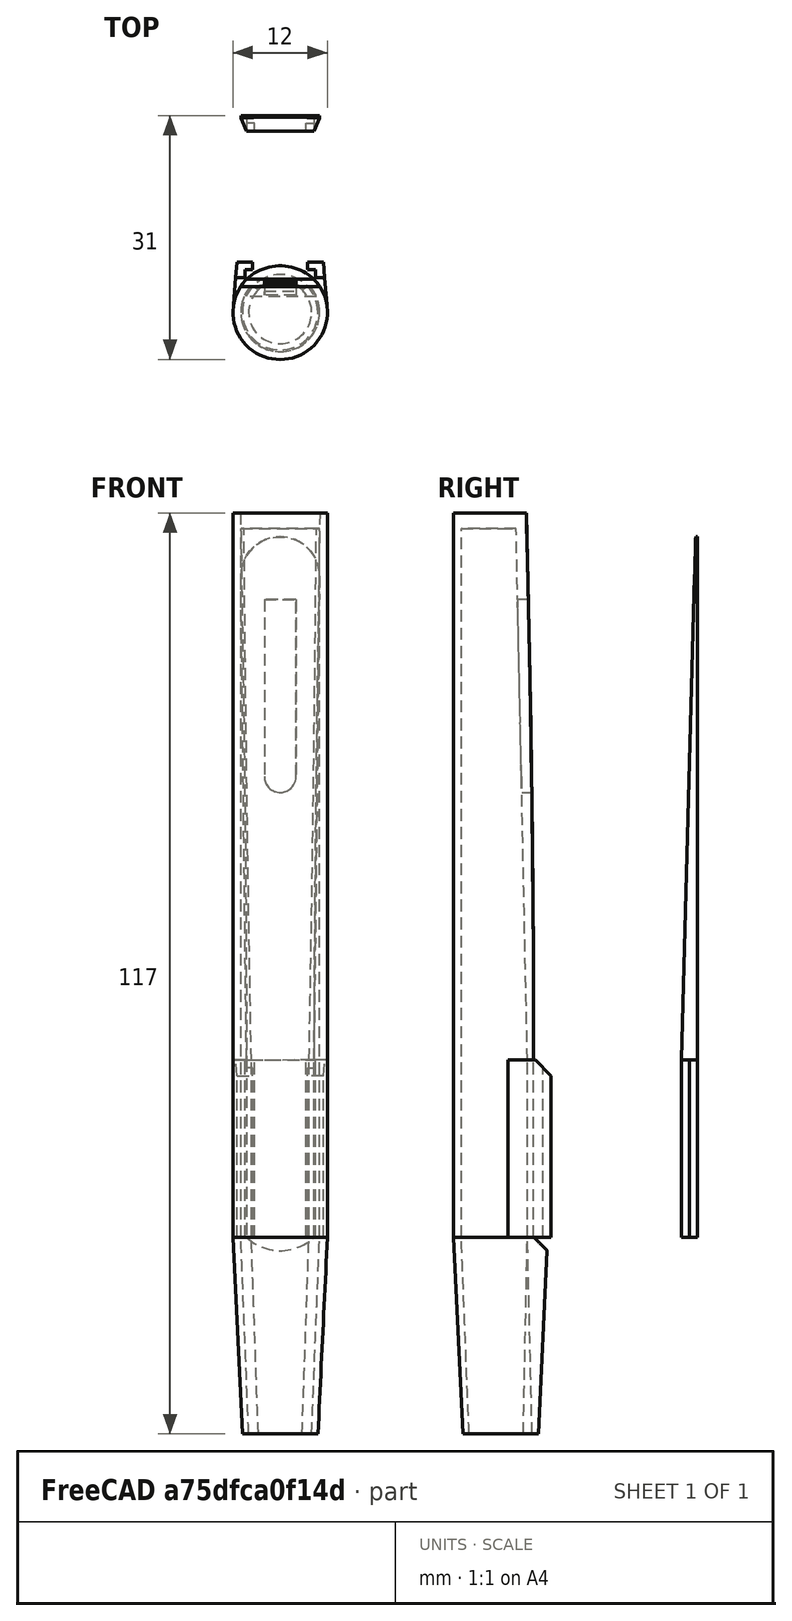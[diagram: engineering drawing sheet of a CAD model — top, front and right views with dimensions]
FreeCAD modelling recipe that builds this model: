
FCSTD DOCUMENT  (FreeCAD 1.0R39319 (Git))
Label: stroik_burd2
License: All rights reserved
LicenseURL: https://en.wikipedia.org/wiki/All_rights_reserved
objects: Sketcher::SketchObject×12, PartDesign::Pocket×6, PartDesign::Pad×4, PartDesign::Body×2, Mesh::Feature×2, Part::FeaturePython×1, PartDesign::FeatureBase×1, App::VarSet×1, PartDesign::Mirrored×1, PartDesign::Plane×1, PartDesign::AdditiveLoft×1, PartDesign::ShapeBinder×1, PartDesign::Chamfer×1
note: 69 computed .brp shape members not serialized (recipe doc carries the construction recipe); baked Part::Feature solids carry a one-line shape summary decoded from their .brp

FEATURE [Part::FeaturePython] Tube  # WARN: FeaturePython — macro-defined, semantics opaque (R4)
  AttacherType = Attacher::AttachEngine3D
  Height = 90
  InnerRadius = 5
  OuterRadius = 6
  Placement = pos=(0,0,0) rot=(0,1,0;1.5708rad)
  expr: Height = VarSet.leaf_len
  expr: InnerRadius = VarSet.d_inner
  expr: OuterRadius = VarSet.d_outer
FEATURE [PartDesign::FeatureBase] BaseFeature
  BaseFeature = -> Tube
  Suppressed = false
FEATURE [App::VarSet] VarSet
  d_inner = 5
  d_outer = 6
  d_outer_plug = 6
  leaf_angle = 0
  leaf_angle2 = 1.55
  leaf_end_thickness = 0.2
  leaf_len = 90
  leaf_start_thickness = 2
  plug_inner_start = 4
  plug_len = 25
  plug_outer_start = 4.8
FEATURE [Sketcher::SketchObject] Sketch
  ArcFitTolerance = 1e-06
  AttachmentSupport = -> [YZ_Plane]
  ExternalGeometry = -> [BaseFeature]
  FullyConstrained = true
  MakeInternals = false
  MapMode = 5
  Placement = pos=(0,0,0) rot=(0.57735,0.57735,0.57735;2.0944rad)
  expr: Constraints[14] = VarSet.leaf_len / 4
  expr: Constraints[8] = VarSet.d_outer * 0.3
  sketch-geometry (6):
    g0: LineSegment StartX=6 StartY=90 StartZ=0 EndX=4.2 EndY=90 EndZ=0
    g1: LineSegment StartX=4.2 StartY=0 StartZ=0 EndX=6 EndY=0 EndZ=0
    g2: LineSegment StartX=6 StartY=0 StartZ=0 EndX=6 EndY=22.5 EndZ=0
    g3: LineSegment StartX=6 StartY=22.5 StartZ=0 EndX=6 EndY=90 EndZ=0
    g4: LineSegment StartX=4.2 StartY=90 StartZ=0 EndX=4.2 EndY=22.5 EndZ=0
    g5: LineSegment StartX=4.2 StartY=22.5 StartZ=0 EndX=4.2 EndY=0 EndZ=0
  constraints (17):
    c: Coincident(g0,g4)
    c: Coincident(g5,g1)
    c: Coincident(g1,g2)
    c: Coincident(g3,g0)
    c: Horizontal(g0)
    c: Horizontal(g1)
    c: Coincident(g0,g-3)
    c: PointOnObject(g5,g-4)
    c: DistanceX(g5,g1) = 1.8
    c: Coincident(g2,g3)
    c: Vertical(g2)
    c: Vertical(g3)
    c: Coincident(g4,g5)
    c: Vertical(g5)
    c: DistanceY(g2,g2) = 22.5
    c: Horizontal(g2,g4)
    c: Vertical(g4)
FEATURE [Sketcher::SketchObject] Sketch001
  ArcFitTolerance = 1e-06
  AttachmentSupport = -> [YZ_Plane]
  ExternalGeometry = -> [Sketch]
  FullyConstrained = true
  MakeInternals = false
  MapMode = 5
  Placement = pos=(0,0,0) rot=(0.57735,0.57735,0.57735;2.0944rad)
  expr: Constraints[12] = 0.8
  expr: Constraints[13] = 3 / 4 * VarSet.leaf_len * tan(VarSet.leaf_angle2) + 0.4 mm
  sketch-geometry (6):
    g0: LineSegment StartX=4.2 StartY=0 StartZ=0 EndX=3.4 EndY=0 EndZ=0
    g1: LineSegment StartX=3.4 StartY=0 StartZ=0 EndX=3.4 EndY=22.5 EndZ=0
    g2: LineSegment StartX=3.4 StartY=22.5 StartZ=0 EndX=1.9735 EndY=90 EndZ=0
    g3: LineSegment StartX=1.9735 StartY=90 StartZ=0 EndX=4.2 EndY=90 EndZ=0
    g4: LineSegment StartX=4.2 StartY=90 StartZ=0 EndX=4.2 EndY=22.5 EndZ=0
    g5: LineSegment StartX=4.2 StartY=22.5 StartZ=0 EndX=4.2 EndY=0 EndZ=0
  constraints (15):
    c: Coincident(g-4,g0)
    c: PointOnObject(g0,g-1)
    c: Coincident(g0,g1)
    c: Vertical(g1)
    c: Coincident(g1,g2)
    c: Coincident(g2,g3)
    c: Coincident(g3,g-3)
    c: Horizontal(g3)
    c: Coincident(g3,g4)
    c: Coincident(g4,g-4)
    c: Coincident(g4,g5)
    c: Coincident(g5,g0)
    c: DistanceX(g1,g4) = 0.8
    c: DistanceX(g2,g3) = 2.2265
    c: Horizontal(g1,g4)
FEATURE [PartDesign::Pocket] Pocket  label="1 ścięcie"
  BaseFeature = -> BaseFeature
  Direction = (-1,0,0)
  Length = 5
  Length2 = 5
  Midplane = true
  Profile = -> Sketch
  ReferenceAxis = -> Sketch [N_Axis]
  Refine = true
  Suppressed = false
  Type = 1
FEATURE [PartDesign::Pad] Pad  label="uzupełnienie"
  AlongSketchNormal = false
  BaseFeature = -> Pocket
  Direction = (1,0,0)
  Length = 13
  Length2 = 10
  Midplane = true
  Profile = -> Sketch001
  ReferenceAxis = -> Sketch001 [N_Axis]
  Refine = true
  Suppressed = false
  Type = 1
  UpToShape = -> [Pocket]
FEATURE [PartDesign::Mirrored] Mirrored
  BaseFeature = -> Pad
  MirrorPlane = -> YZ_Plane
  Originals = -> [Pad]
  Refine = true
  Suppressed = false
  TransformMode = 0
FEATURE [Sketcher::SketchObject] Sketch002
  ArcFitTolerance = 1e-06
  AttachmentSupport = -> [Mirrored]
  ExternalGeometry = -> [Mirrored]
  FullyConstrained = true
  MakeInternals = false
  MapMode = 5
  Placement = pos=(0,4.2,0) rot=(0,0.707107,0.707107;3.14159rad)
  expr: Constraints[10] = 3 / 4 * VarSet.leaf_len / 3
  expr: Constraints[6] = VarSet.d_outer / 3
  expr: Constraints[9] = VarSet.leaf_len / 10
  sketch-geometry (4):
    g0: LineSegment StartX=2.011 StartY=58.5 StartZ=0 EndX=2.011 EndY=81 EndZ=0
    g1: LineSegment StartX=2.011 StartY=81 StartZ=0 EndX=-2.011 EndY=81 EndZ=0
    g2: LineSegment StartX=-2.011 StartY=81 StartZ=0 EndX=-2.011 EndY=58.5 EndZ=0
    g3: ArcOfCircle CenterX=0 CenterY=58.5 CenterZ=0 NormalX=0 NormalY=0 NormalZ=1 AngleXU=0 Radius=2.011 StartAngle=3.14159 EndAngle=6.28319
  constraints (12):
    c: Coincident(g0,g1)
    c: Coincident(g1,g2)
    c: Coincident(g3,g2)
    c: Coincident(g3,g0)
    c: PointOnObject(g3,g-2)
    c: Horizontal(g0,g2)
    c: DistanceX(g0,g-4) = 2
    c: Horizontal(g2,g3)
    c: Symmetric(g0,g1,g-2)
    c: DistanceY(g1,g-7) = 9
    c: DistanceY(g3,g1) = 22.5
    c: Vertical(g1,g2)
FEATURE [PartDesign::Pocket] Pocket001  label="dziurka"
  BaseFeature = -> Mirrored
  Direction = (0,-1,2e-16)
  Length = 2.5
  Length2 = 5
  Profile = -> Sketch002
  ReferenceAxis = -> Sketch002 [N_Axis]
  Refine = true
  Suppressed = false
  Type = 0
  expr: Length = VarSet.d_inner / 2
FEATURE [Sketcher::SketchObject] Sketch003
  ArcFitTolerance = 1e-06
  AttachmentSupport = -> [Pocket001]
  ExternalGeometry = -> [Pocket001]
  FullyConstrained = true
  MakeInternals = false
  MapMode = 5
  Placement = pos=(0,0,90) rot=(0,0,1;0rad)
  sketch-geometry (2):
    g0: ArcOfCircle CenterX=0 CenterY=0 CenterZ=0 NormalX=0 NormalY=0 NormalZ=1 AngleXU=0 Radius=6 StartAngle=2.3662 EndAngle=7.05858
    g1: LineSegment StartX=-4.28486 StartY=4.2 StartZ=0 EndX=4.28486 EndY=4.2 EndZ=0
  constraints (5):
    c: Coincident(g0,g-1)
    c: Coincident(g0,g-4)
    c: Coincident(g1,g0)
    c: Coincident(g1,g0)
    c: Horizontal(g1)
FEATURE [PartDesign::Pad] Pad001  label="zaślepka"
  BaseFeature = -> Pocket001
  Direction = (0,0,1)
  Length = 2
  Length2 = 10
  Profile = -> Sketch003
  ReferenceAxis = -> Sketch003 [N_Axis]
  Refine = true
  Suppressed = false
  Type = 0
FEATURE [Sketcher::SketchObject] Sketch004
  ArcFitTolerance = 1e-06
  AttachmentSupport = -> [Pad001]
  ExternalGeometry = -> [Pad001]
  FullyConstrained = true
  MakeInternals = false
  MapMode = 5
  Placement = pos=(0,0,0) rot=(1,0,0;3.14159rad)
  expr: Constraints[4] = VarSet.d_outer_plug
  expr: Constraints[7] = VarSet.d_inner
  sketch-geometry (3):
    g0: ArcOfCircle CenterX=0 CenterY=0 CenterZ=0 NormalX=0 NormalY=0 NormalZ=1 AngleXU=0 Radius=5 StartAngle=5.53542 EndAngle=10.1725
    g1: LineSegment StartX=-3.66606 StartY=-3.4 StartZ=0 EndX=3.66606 EndY=-3.4 EndZ=0
    g2: Circle CenterX=0 CenterY=0 CenterZ=0 NormalX=0 NormalY=0 NormalZ=1 AngleXU=0 Radius=6
  constraints (8):
    c: Coincident(g1,g0)
    c: Horizontal(g1)
    c: Coincident(g2,g0)
    c: Coincident(g-1,g0)
    c: Radius(g2) = 6
    c: Horizontal(g0,g-6)
    c: Coincident(g1,g0)
    c: Radius(g0) = 5
FEATURE [PartDesign::Plane] DatumPlane
  AttachmentOffset = pos=(0,0,25) rot=(0,0,1;0rad)
  AttachmentSupport = -> [Pocket001]
  Length = 60
  MapMode = 5
  Placement = pos=(0,0,-25) rot=(1,0,0;3.14159rad)
  ResizeMode = 0
  Width = 60
  expr: .AttachmentOffset.Base.z = VarSet.plug_len
FEATURE [Sketcher::SketchObject] Sketch005
  ArcFitTolerance = 1e-06
  AttachmentSupport = -> [DatumPlane]
  ExternalGeometry = -> [Sketch004,Pad001]
  FullyConstrained = true
  MakeInternals = false
  MapMode = 5
  Placement = pos=(0,0,-25) rot=(1,0,0;3.14159rad)
  expr: Constraints[2] = VarSet.plug_inner_start
  expr: Constraints[3] = VarSet.plug_outer_start
  sketch-geometry (2):
    g0: Circle CenterX=0 CenterY=0 CenterZ=0 NormalX=0 NormalY=0 NormalZ=1 AngleXU=0 Radius=4
    g1: Circle CenterX=0 CenterY=0 CenterZ=0 NormalX=0 NormalY=0 NormalZ=1 AngleXU=0 Radius=4.8
  constraints (4):
    c: Coincident(g0,g-1)
    c: Coincident(g1,g0)
    c: Radius(g0) = 4
    c: Radius(g1) = 4.8
FEATURE [PartDesign::AdditiveLoft] AdditiveLoft  label="dziubek"
  BaseFeature = -> Pad001
  Closed = false
  Profile = -> Sketch005
  Refine = true
  Ruled = false
  Sections = -> [Sketch004]
  Suppressed = false
FEATURE [Sketcher::SketchObject] Sketch006
  ArcFitTolerance = 1e-06
  AttachmentSupport = -> [Pad001]
  ExternalGeometry = -> [Pad001]
  FullyConstrained = true
  MakeInternals = false
  MapMode = 5
  Placement = pos=(0,0,0) rot=(1,0,0;3.14159rad)
  sketch-geometry (14):
    g0: LineSegment StartX=4.28486 StartY=-4.2 StartZ=0 EndX=6 EndY=0 EndZ=0
    g1: LineSegment StartX=6 StartY=0 StartZ=0 EndX=5.48486 EndY=-6.4 EndZ=0
    g2: LineSegment StartX=5.48486 StartY=-6.4 StartZ=0 EndX=3.48486 EndY=-6.4 EndZ=0
    g3: LineSegment StartX=3.48486 StartY=-6.4 StartZ=0 EndX=3.48486 EndY=-5.4 EndZ=0
    g4: LineSegment StartX=3.48486 StartY=-5.4 StartZ=0 EndX=4.48486 EndY=-5.4 EndZ=0
    g5: LineSegment StartX=-5.48486 StartY=-6.4 StartZ=0 EndX=-3.48486 EndY=-6.4 EndZ=0
    g6: LineSegment StartX=-6 StartY=0 StartZ=0 EndX=-5.48486 EndY=-6.4 EndZ=0
    g7: LineSegment StartX=-4.28486 StartY=-4.2 StartZ=0 EndX=-6 EndY=0 EndZ=0
    g8: LineSegment StartX=-3.48486 StartY=-5.4 StartZ=0 EndX=-4.48486 EndY=-5.4 EndZ=0
    g9: LineSegment StartX=-3.48486 StartY=-6.4 StartZ=0 EndX=-3.48486 EndY=-5.4 EndZ=0
    g10: LineSegment StartX=4.48486 StartY=-5.4 StartZ=0 EndX=4.48486 EndY=-4.2 EndZ=0
    g11: LineSegment StartX=4.48486 StartY=-4.2 StartZ=0 EndX=4.28486 EndY=-4.2 EndZ=0
    g12: LineSegment StartX=-4.48486 StartY=-5.4 StartZ=0 EndX=-4.48486 EndY=-4.2 EndZ=0
    g13: LineSegment StartX=-4.48486 StartY=-4.2 StartZ=0 EndX=-4.28486 EndY=-4.2 EndZ=0
  constraints (34):
    c: Coincident(g-5,g0)
    c: Coincident(g0,g1)
    c: Coincident(g1,g2)
    c: Horizontal(g2)
    c: Coincident(g2,g3)
    c: Vertical(g3)
    c: Coincident(g3,g4)
    c: Horizontal(g4)
    c: Coincident(g4,g10)
    c: Coincident(g11,g0)
    c: Coincident(g7,g6)
    c: Coincident(g6,g5)
    c: Coincident(g5,g9)
    c: Vertical(g9)
    c: Coincident(g9,g8)
    c: Horizontal(g8)
    c: Coincident(g8,g12)
    c: Coincident(g13,g7)
    c: Symmetric(g2,g5,g-2)
    c: DistanceX(g4,g4) = 1
    c: Symmetric(g4,g12,g-2)
    c: Symmetric(g0,g6,g-2)
    c: DistanceY(g3,g3) = 1
    c: Symmetric(g7,g0,g-2)
    c: DistanceY(g10,g11) = 1.2
    c: DistanceX(g2,g2) = 2
    c: Coincident(g0,g-5)
    c: Symmetric(g5,g1,g-2)
    c: Coincident(g10,g11)
    c: Vertical(g10)
    c: Horizontal(g10,g0)
    c: DistanceX(g11,g11) = 0.2
    c: Coincident(g12,g13)
    c: Symmetric(g12,g10,g-2)
FEATURE [PartDesign::Pad] Pad002  label="uchwyt na listek"
  BaseFeature = -> AdditiveLoft
  Direction = (0,0,-1)
  Length = 22.5
  Length2 = 10
  Profile = -> Sketch006
  ReferenceAxis = -> Sketch006 [N_Axis]
  Refine = true
  Reversed = true
  Suppressed = false
  Type = 0
  expr: Length = VarSet.leaf_len / 4
FEATURE [Sketcher::SketchObject] Sketch009
  ArcFitTolerance = 1e-06
  AttachmentSupport = -> [YZ_Plane]
  ExternalGeometry = -> [Pad001]
  FullyConstrained = true
  MakeInternals = false
  MapMode = 5
  Placement = pos=(0,0,0) rot=(0.57735,0.57735,0.57735;2.0944rad)
  expr: Constraints[12] = VarSet.leaf_len * 2
  expr: Constraints[15] = 90 deg - VarSet.leaf_angle2
  expr: Constraints[1] = VarSet.leaf_len / 4
  sketch-geometry (11):
    g0: GeomPoint X=4.2 Y=22.5 Z=0
    g1: Circle [constr] CenterX=4.2 CenterY=22.5 CenterZ=0 NormalX=0 NormalY=0 NormalZ=1 AngleXU=0 Radius=1
    g2: Circle [constr] CenterX=4.2 CenterY=92 CenterZ=0 NormalX=0 NormalY=0 NormalZ=1 AngleXU=0 Radius=1
    g3: Circle [constr] CenterX=-0.0618247 CenterY=180 CenterZ=0 NormalX=0 NormalY=0 NormalZ=1 AngleXU=0 Radius=1
    g4: BSplineCurve PolesCount=3 KnotsCount=2 Degree=2 IsPeriodic=0
    g5: GeomPoint [constr] X=4.2 Y=22.5 Z=0
    g6: GeomPoint [constr] X=-0.0618247 Y=180 Z=0
    g7: LineSegment [constr] StartX=-0.0618247 StartY=180 StartZ=0 EndX=4.2 EndY=22.5 EndZ=0
    g8: LineSegment StartX=-0.0618247 StartY=180 StartZ=0 EndX=104.2 EndY=180 EndZ=0
    g9: LineSegment StartX=104.2 StartY=180 StartZ=0 EndX=104.2 EndY=22.5 EndZ=0
    g10: LineSegment StartX=104.2 StartY=22.5 StartZ=0 EndX=4.2 EndY=22.5 EndZ=0
  constraints (24):
    c: PointOnObject(g0,g-3)
    c: DistanceY(g-3,g0) = 22.5
    c: Weight(g1) = 1
    c: Equal(g1,g2)
    c: Equal(g1,g3)
    c: InternalAlignment(g1,g4)
    c: InternalAlignment(g2,g4)
    c: InternalAlignment(g3,g4)
    c: InternalAlignment(g5,g4)
    c: InternalAlignment(g6,g4)
    c: Coincident(g1,g0)
    c: Coincident(g2,g-3)
    c: DistanceY(g-1,g4) = 180
    c: Coincident(g7,g4)
    c: Coincident(g7,g4)
    c: Angle(g7,g-1) = 1.54374
    c: Coincident(g8,g4)
    c: Horizontal(g8)
    c: Coincident(g8,g9)
    c: Vertical(g9)
    c: Coincident(g9,g10)
    c: Coincident(g10,g0)
    c: Horizontal(g10)
    c: DistanceX(g10,g10) = 100
FEATURE [PartDesign::Pocket] Pocket003  label="2 ścięcie"
  BaseFeature = -> Pad002
  Direction = (-1,0,0)
  Length = 100
  Length2 = 5
  Midplane = true
  Profile = -> Sketch009
  ReferenceAxis = -> Sketch009 [N_Axis]
  Refine = true
  Suppressed = false
  Type = 0
FEATURE [PartDesign::ShapeBinder] ShapeBinder
  Support = -> [Mirrored]
  TraceSupport = false
FEATURE [Sketcher::SketchObject] Sketch010
  ArcFitTolerance = 1e-06
  AttachmentSupport = -> [XZ_Plane001]
  ExternalGeometry = -> [ShapeBinder]
  FullyConstrained = true
  MakeInternals = false
  MapMode = 5
  Placement = pos=(0,0,0) rot=(1,0,0;1.5708rad)
  expr: Constraints[10] = VarSet.d_inner * 2
  expr: Constraints[6] = VarSet.leaf_len / 4
  expr: Constraints[9] = VarSet.leaf_len - VarSet.d_outer
  sketch-geometry (6):
    g0: LineSegment StartX=-4.28486 StartY=0 StartZ=0 EndX=4.28486 EndY=9e-16 EndZ=0
    g1: LineSegment StartX=4.28486 StartY=9e-16 StartZ=0 EndX=4.28486 EndY=22.5 EndZ=0
    g2: LineSegment StartX=-4.28486 StartY=22.5 StartZ=0 EndX=-4.28486 EndY=0 EndZ=0
    g3: LineSegment StartX=4.28486 StartY=22.5 StartZ=0 EndX=5 EndY=84 EndZ=0
    g4: LineSegment StartX=-4.28486 StartY=22.5 StartZ=0 EndX=-5 EndY=84 EndZ=0
    g5: ArcOfCircle CenterX=1.364e-13 CenterY=84 CenterZ=0 NormalX=0 NormalY=0 NormalZ=1 AngleXU=0 Radius=5 StartAngle=2e-16 EndAngle=3.14159
  constraints (16):
    c: Coincident(g0,g1)
    c: Coincident(g2,g0)
    c: Vertical(g1)
    c: Vertical(g2)
    c: Coincident(g0,g-3)
    c: Coincident(g0,g-3)
    c: DistanceY(g1,g1) = 22.5
    c: Coincident(g3,g1)
    c: Symmetric(g3,g4,g-2)
    c: DistanceY(g0,g3) = 84
    c: DistanceX(g4,g3) = 10
    c: Coincident(g5,g3)
    c: Coincident(g5,g4)
    c: Horizontal(g5,g3)
    c: Horizontal(g2,g1)
    c: Coincident(g4,g2)
FEATURE [PartDesign::Pad] Pad003
  Direction = (0,-1,2e-16)
  Length = 2
  Length2 = 10
  Placement = pos=(0,0,0) rot=(1,0,0;1.5708rad)
  Profile = -> Sketch010
  ReferenceAxis = -> Sketch010 [N_Axis]
  Refine = true
  Suppressed = false
  Type = 0
  expr: Length = VarSet.leaf_start_thickness
FEATURE [Sketcher::SketchObject] Sketch011
  ArcFitTolerance = 1e-06
  AttachmentSupport = -> [Pad003]
  ExternalGeometry = -> [Pad003]
  FullyConstrained = true
  MakeInternals = false
  MapMode = 5
  Placement = pos=(0,0,4e-16) rot=(1,0,0;3.14159rad)
  sketch-geometry (8):
    g0: LineSegment StartX=-3.28486 StartY=2 StartZ=0 EndX=-3.28486 EndY=1 EndZ=0
    g1: LineSegment StartX=-3.28486 StartY=1 StartZ=0 EndX=-8.28486 EndY=1 EndZ=0
    g2: LineSegment StartX=-8.28486 StartY=1 StartZ=0 EndX=-8.28486 EndY=5.50104 EndZ=0
    g3: LineSegment StartX=-8.28486 StartY=5.50104 StartZ=0 EndX=-3.28486 EndY=2 EndZ=0
    g4: LineSegment StartX=8.28486 StartY=5.50104 StartZ=0 EndX=3.28486 EndY=2 EndZ=0
    g5: LineSegment StartX=3.28486 StartY=2 StartZ=0 EndX=3.28486 EndY=1 EndZ=0
    g6: LineSegment StartX=3.28486 StartY=1 StartZ=0 EndX=8.28486 EndY=1 EndZ=0
    g7: LineSegment StartX=8.28486 StartY=1 StartZ=0 EndX=8.28486 EndY=5.50104 EndZ=0
  constraints (21):
    c: PointOnObject(g0,g-3)
    c: Vertical(g0)
    c: Coincident(g0,g1)
    c: Horizontal(g1)
    c: Coincident(g1,g2)
    c: Vertical(g2)
    c: Coincident(g2,g3)
    c: Coincident(g3,g0)
    c: DistanceX(g-4,g0) = 1
    c: Vertical(g5)
    c: Coincident(g5,g6)
    c: Coincident(g6,g7)
    c: Coincident(g7,g4)
    c: Coincident(g4,g5)
    c: Symmetric(g4,g0,g-2)
    c: Symmetric(g5,g0,g-2)
    c: Symmetric(g6,g1,g-2)
    c: Symmetric(g4,g2,g-2)
    c: DistanceY(g-5,g0) = 1
    c: Angle(g-3,g3) = 2.53073
    c: DistanceX(g1,g1) = 5
FEATURE [PartDesign::Pocket] Pocket004  label="uchwyt"
  BaseFeature = -> Pad003
  Direction = (0,0,1)
  Length = 22.5
  Length2 = 5
  Placement = pos=(0,0,0) rot=(1,0,0;1.5708rad)
  Profile = -> Sketch011
  ReferenceAxis = -> Sketch011 [N_Axis]
  Refine = true
  Suppressed = false
  Type = 0
  expr: Length = VarSet.leaf_len / 4
FEATURE [Sketcher::SketchObject] Sketch012
  ArcFitTolerance = 1e-06
  AttachmentSupport = -> [Pocket004]
  ExternalGeometry = -> [Pocket004]
  FullyConstrained = true
  MakeInternals = false
  MapMode = 5
  Placement = pos=(-4.02268,0,-0.046777) rot=(0.711206,0,-0.702984;3.14159rad)
  expr: Constraints[0] = VarSet.d_inner + 0.4 mm
  expr: Constraints[5] = VarSet.leaf_end_thickness
  sketch-geometry (3):
    g0: LineSegment StartX=-89.4525 StartY=0.2 StartZ=0 EndX=-22.5483 EndY=2 EndZ=0
    g1: LineSegment StartX=-89.4525 StartY=0.2 StartZ=0 EndX=-89.4525 EndY=14.03 EndZ=0
    g2: LineSegment StartX=-89.4525 StartY=14.03 StartZ=0 EndX=-22.5483 EndY=2 EndZ=0
  constraints (8):
    c: DistanceX(g0,g-3) = 5.4
    c: Coincident(g1,g0)
    c: Vertical(g1)
    c: Coincident(g2,g1)
    c: Coincident(g2,g0)
    c: DistanceY(g-4,g0) = 0.2
    c: Coincident(g0,g-3)
    c: DistanceY(g1,g1) = 13.83
FEATURE [PartDesign::Pocket] Pocket005  label="Pochylenie"
  BaseFeature = -> Pocket004
  Direction = (0.999932,0,0.0116276)
  Length = 5
  Length2 = 5
  Placement = pos=(0,0,0) rot=(1,0,0;1.5708rad)
  Profile = -> Sketch012
  ReferenceAxis = -> Sketch012 [N_Axis]
  Refine = true
  Suppressed = false
  Type = 1
FEATURE [PartDesign::Body] Body001  label="listek"
  AllowCompound = false
  Group = -> [ShapeBinder,Sketch010,Pad003,Sketch011,Pocket004,Sketch012,Pocket005]
  Origin = -> Origin001
  Placement = pos=(0,25,0) rot=(0,0,1;0rad)
  Tip = -> Pocket005
FEATURE [PartDesign::Chamfer] Chamfer
  Angle = 45
  Base = -> Pocket003 [Edge85,Edge73]
  BaseFeature = -> Pocket003
  ChamferType = 0
  FlipDirection = false
  Refine = true
  Size = 2
  Size2 = 1
  SupportTransform = false
  Suppressed = false
  UseAllEdges = false
FEATURE [Sketcher::SketchObject] Sketch013
  ArcFitTolerance = 1e-06
  AttachmentSupport = -> [YZ_Plane]
  ExternalGeometry = -> [AdditiveLoft]
  FullyConstrained = true
  MakeInternals = false
  MapMode = 5
  Placement = pos=(0,0,0) rot=(0.57735,0.57735,0.57735;2.0944rad)
  sketch-geometry (3):
    g0: LineSegment StartX=4.2 StartY=0 StartZ=0 EndX=18.3421 EndY=-14.1421 EndZ=0
    g1: LineSegment StartX=18.3421 StartY=-14.1421 StartZ=0 EndX=18.3421 EndY=1.8e-15 EndZ=0
    g2: LineSegment StartX=18.3421 StartY=1.8e-15 StartZ=0 EndX=4.2 EndY=0 EndZ=0
  constraints (8):
    c: Coincident(g-3,g0)
    c: Coincident(g0,g1)
    c: Vertical(g1)
    c: Coincident(g1,g2)
    c: Coincident(g2,g0)
    c: Angle(g-2,g0) = 0.785398
    c: Distance(g0,g0) = 20
    c: Angle(g0,g2) = 0.785398
FEATURE [PartDesign::Pocket] Pocket006
  BaseFeature = -> Chamfer
  Direction = (-1,0,0)
  Length = 5
  Length2 = 5
  Midplane = true
  Profile = -> Sketch013
  ReferenceAxis = -> Sketch013 [N_Axis]
  Refine = true
  Suppressed = false
  Type = 1
FEATURE [PartDesign::Body] Body  label="stroik"
  AllowCompound = false
  BaseFeature = -> Tube
  Group = -> [BaseFeature,Sketch,Pocket,Sketch001,Pad,Mirrored,Sketch002,Pocket001,Sketch003,Pad001,Sketch004,DatumPlane,Sketch005,AdditiveLoft,Sketch006,Pad002,Sketch009,Pocket003,Chamfer,Sketch013,Pocket006]
  Origin = -> Origin
  Tip = -> Pocket006
FEATURE [Mesh::Feature] Mesh  label="listek (Meshed)"
FEATURE [Mesh::Feature] Mesh001  label="stroik (Meshed)"
